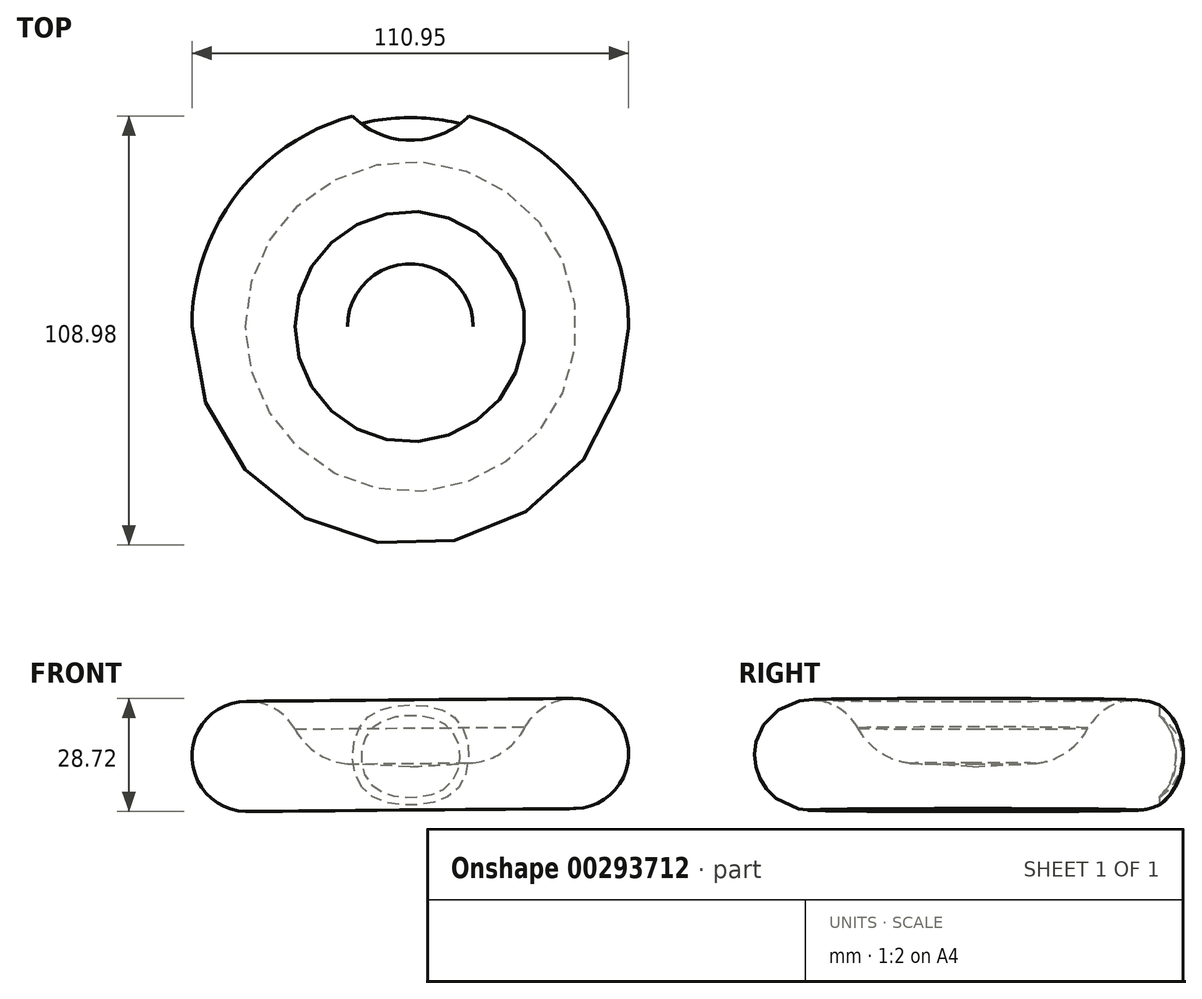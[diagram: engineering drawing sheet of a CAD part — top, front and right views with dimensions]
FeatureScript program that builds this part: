
annotation { "Feature Type Name" : "Feature", "Feature Type Description" : "" }
export const myFeature = defineFeature(function(context is Context, id is Id, definition is map)
    precondition{}
    {
        {
            var Q0;
            Q0=qCreatedBy(makeId("Front.planeOp"),FACE);
            var sketch = newSketch(context, id + "F0", { "sketchPlane" : qUnion([Q0])});
            skArc(sketch, "E0", {"start": v(-29.26, 20.25) * mm, "mid": v(-53.5, 20.99) * mm, "end": v(-42, -0.37) * mm});
            skArc(sketch, "E1", {"start": v(-29.44, 20.58) * mm, "mid": v(-23.87, 14.48) * mm, "end": v(-16.08, 11.72) * mm});
            skLineSegment(sketch, "E2", {"start": v(-42, -0.37) * mm, "end": v(0, 0) * mm});
            skLineSegment(sketch, "E3", {"start": v(0, 0) * mm, "end": v(-0.1, 11) * mm});
            skLineSegment(sketch, "E4", {"start": v(-0.1, 11) * mm, "end": v(-16.08, 11.72) * mm});
            skSolve(sketch);
        }
        {
            var Q0;
            {var subQ0=sQuery(id+"F0.wireOp",EDGE,"E2");Q0=makeQuery(id+"F0.imprint","IMPRINT",FACE,{"disambiguationData":[TD([[makeQuery(id+"F0.imprint","IMPRINT",EDGE,{"derivedFrom":subQ0}),1.0]])]});}
            var Q1;
            Q1=sQuery(id+"F0.wireOp",EDGE,"E3");
            revolve(context, id + "F1", {"entities" : qUnion([Q0]), "axis" : qUnion([Q1]), "revolveType" : RevolveType.FULL});
        }
        {
            var Q0;
            Q0=qCreatedBy(makeId("Top.planeOp"),FACE);
            var sketch = newSketch(context, id + "F2", { "sketchPlane" : qUnion([Q0])});
            skCircle(sketch, "E5", {"center": v(0, 68.05) * mm, "radius": 20.73 * mm});
            skSolve(sketch);
        }
        {
            var Q0;
            Q0 = qSketchRegion(id + "F2", true);
            extrude(context, id + "F3", {"entities" : qUnion([Q0]), "operationType" : NewBodyOperationType.REMOVE, "depth" : 43.7 * mm});
        }
        {
            var Q0;
            Q0=qCreatedBy(makeId("Front.planeOp"),FACE);
            var sketch = newSketch(context, id + "F4", { "sketchPlane" : qUnion([Q0])});
            skCircle(sketch, "E6", {"center": v(-41, 13.24) * mm, "radius": 12.21 * mm});
            skSolve(sketch);
        }
        {
            var Q0;
            Q0 = qSketchRegion(id + "F4", true);
            var Q1;
            Q1=sQuery(id+"F0.wireOp",EDGE,"E3");
            revolve(context, id + "F5", {"operationType" : NewBodyOperationType.ADD, "entities" : qUnion([Q0]), "axis" : qUnion([Q1]), "revolveType" : RevolveType.FULL});
        }
    });
